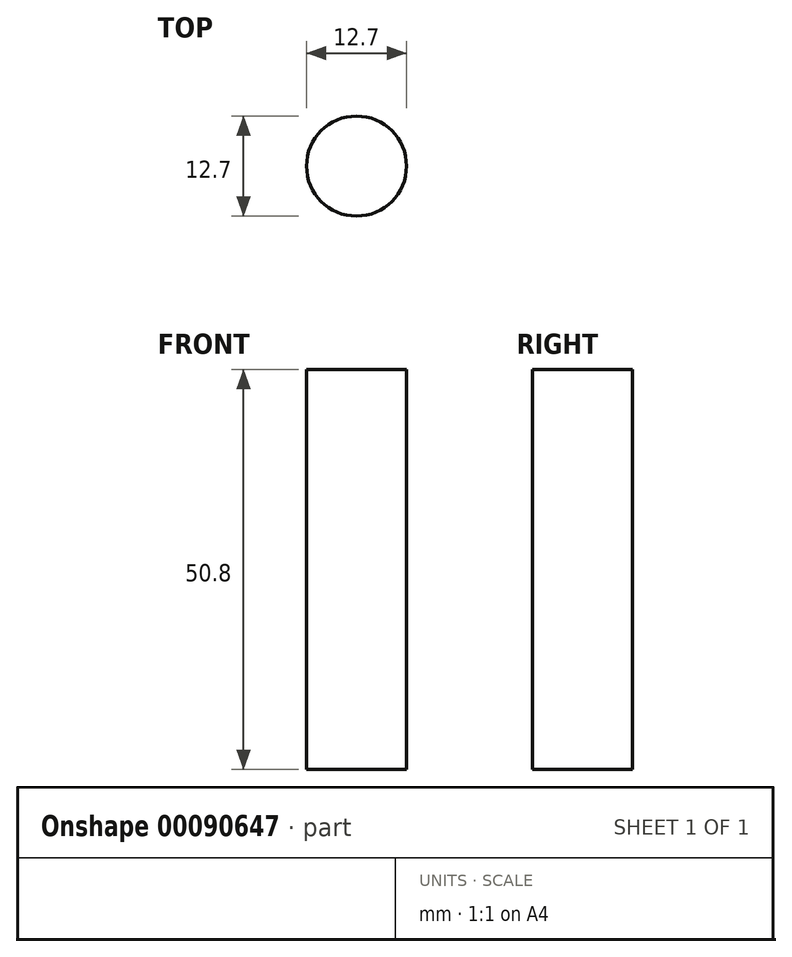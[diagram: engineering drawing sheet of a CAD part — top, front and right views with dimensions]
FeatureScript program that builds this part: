
annotation { "Feature Type Name" : "Feature", "Feature Type Description" : "" }
export const myFeature = defineFeature(function(context is Context, id is Id, definition is map)
    precondition{}
    {
        {
            var Q0;
            Q0=qCreatedBy(makeId("Top.planeOp"),FACE);
            var sketch = newSketch(context, id + "F0", { "sketchPlane" : qUnion([Q0])});
            skCircle(sketch, "E0", {"center": v(-100.97, -3.93) * mm, "radius": 6.35 * mm});
            skSolve(sketch);
        }
        {
            var Q0;
            Q0=makeQuery(id+"F0.imprint","IMPRINT",FACE,{"disambiguationData":[TD([[makeQuery(id+"F0.imprint","IMPRINT",EDGE,{"derivedFrom":sQuery(id+"F0.wireOp",EDGE,"E0")}),1.0]])]});
            extrude(context, id + "F1", {"entities" : qUnion([Q0]), "depth" : 50.8 * mm});
        }
    });
